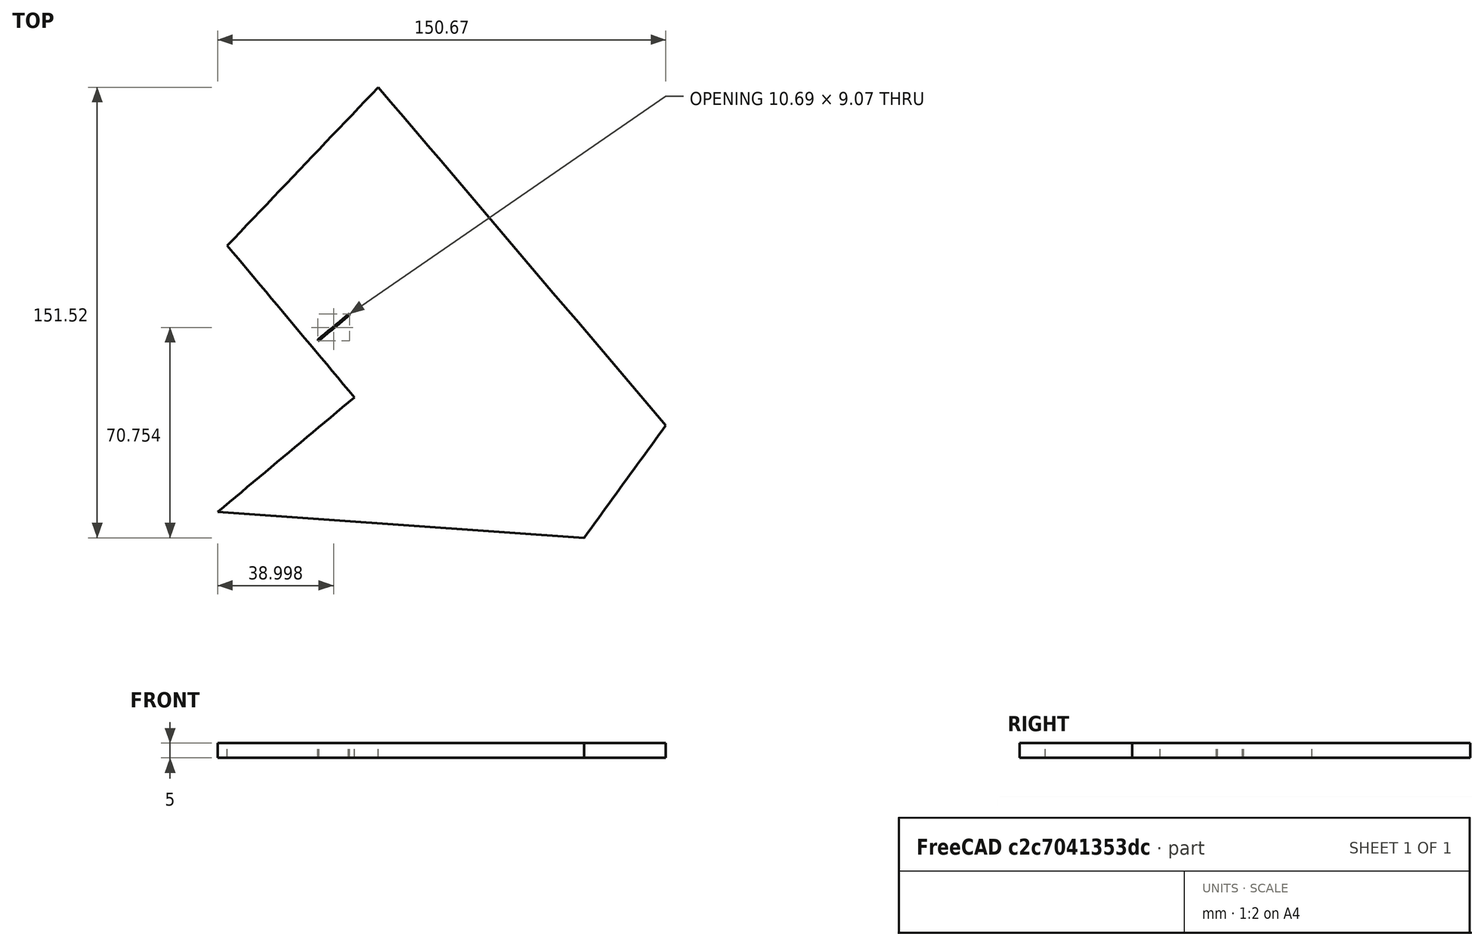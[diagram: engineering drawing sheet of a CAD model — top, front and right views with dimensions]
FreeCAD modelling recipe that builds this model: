
FCSTD DOCUMENT  (FreeCAD 0.19R)
Label: F-35_v2_parts_17
License: All rights reserved
LicenseURL: http://en.wikipedia.org/wiki/All_rights_reserved
objects: App::DocumentObjectGroup×2, PartDesign::CoordinateSystem×2, App::FeaturePython×1, Sketcher::SketchObject×1, PartDesign::Pad×1, PartDesign::Body×1, App::Part×1
note: 6 computed .brp shape members not serialized (recipe doc carries the construction recipe); baked Part::Feature solids carry a one-line shape summary decoded from their .brp

FEATURE [App::DocumentObjectGroup] Parts
FEATURE [PartDesign::CoordinateSystem] LCS_Origin
  AttacherType = Attacher::AttachEngine3D
  MapMode = 2
  Support = -> [X_Axis]
FEATURE [App::DocumentObjectGroup] Constraints
FEATURE [App::FeaturePython] Variables  # WARN: FeaturePython — macro-defined, semantics opaque (R4)
FEATURE [Sketcher::SketchObject] Sketch004
  FullyConstrained = false
  sketch-geometry (10):
    g0: BSplineCurve PolesCount=2 KnotsCount=2 Degree=1 IsPeriodic=0
    g1: BSplineCurve PolesCount=2 KnotsCount=2 Degree=1 IsPeriodic=0
    g2: BSplineCurve PolesCount=2 KnotsCount=2 Degree=1 IsPeriodic=0
    g3: BSplineCurve PolesCount=2 KnotsCount=2 Degree=1 IsPeriodic=0
    g4: BSplineCurve PolesCount=2 KnotsCount=2 Degree=1 IsPeriodic=0
    g5: BSplineCurve PolesCount=2 KnotsCount=2 Degree=1 IsPeriodic=0
    g6: BSplineCurve PolesCount=2 KnotsCount=2 Degree=1 IsPeriodic=0
    g7: BSplineCurve PolesCount=2 KnotsCount=2 Degree=1 IsPeriodic=0
    g8: BSplineCurve PolesCount=2 KnotsCount=2 Degree=1 IsPeriodic=0
    g9: BSplineCurve PolesCount=2 KnotsCount=2 Degree=1 IsPeriodic=0
FEATURE [PartDesign::Pad] Pad002
  Direction = (1,1,1)
  Length = 5
  Length2 = 100
  Profile = -> Sketch004
  Type = 0
FEATURE [PartDesign::Body] Body004  label="Part17"
  Group = -> [Sketch004,Pad002]
  Origin = -> Origin005
  Tip = -> Pad002
FEATURE [PartDesign::CoordinateSystem] LCS_1
  AttacherType = Attacher::AttachEngine3D
  MapMode = 7
  Placement = pos=(476.026,-308.838,0) rot=(0.889401,0.323238,0.323238;1.68773rad)
  Support = -> [Pad002]
FEATURE [App::Part] Model
  Configuration = 0
  Group = -> [LCS_Origin,Constraints,Variables,Body004,LCS_1]
  Origin = -> Origin
  Type = Assembly4 Model
